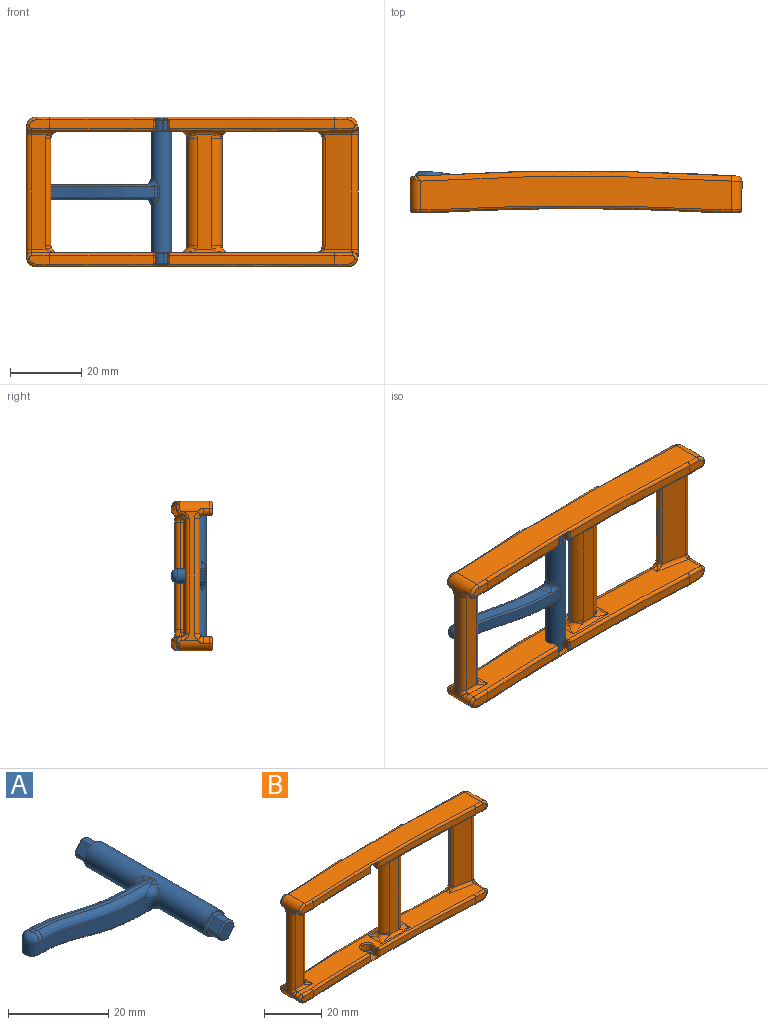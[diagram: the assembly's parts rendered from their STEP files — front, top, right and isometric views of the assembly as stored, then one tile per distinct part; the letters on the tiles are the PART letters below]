
ASSEMBLY  parts=2 mates=1
PART A: 70 faces, bbox 55.5x40.7x10.1 mm
  f0: cylinder r=2.9mm len=33.8mm, axis (0,1,0), area 564.6mm2, adj f1,f2,f36,f37,f38,f39,f40,f41
  f1: plane 5.8x5.8mm, normal (0,-1,0), area 5.9mm2, adj f0,f54,f56,f57,f59,f60,f61
  f2: plane 5.8x5.8mm, normal (0,1,0), area 5.9mm2, adj f0,f62,f63,f64,f65
  f3: plane 3.75x3.75mm, normal (0,1,0), area 9.4mm2, adj f66,f67,f68,f69
  f4: cylinder r=2.27mm len=2.76mm, axis (0,1,0), area 11mm2, adj f5,f7,f64,f67
  f5: plane 2.65x2.13mm, normal (-0.77,0,0.64), area 7.4mm2, adj f4,f6,f62,f69
  f6: cylinder r=2.27mm len=2.76mm, axis (0,1,0), area 11mm2, adj f5,f7,f63,f68
  f7: plane 2.65x2.13mm, normal (0.77,0,-0.64), area 7.4mm2, adj f4,f6,f65,f66
  f8: plane 2.65x2.02mm, normal (0.77,0,-0.64), area 7mm2, adj f9,f53,f58,f61
  f9: cylinder r=2.27mm len=2.76mm, axis (0,1,0), area 11mm2, adj f8,f10,f50,f59
  f10: plane 2.65x2.02mm, normal (-0.77,0,0.64), area 7mm2, adj f9,f48,f51,f56
  f11: cylinder r=2.27mm len=2.65mm, axis (0,1,0), area 10.2mm2, adj f51,f52,f57,f58
  f12: plane 3.75x3.75mm, normal (0,-1,0), area 9.4mm2, adj f48,f50,f52,f53
  f13: plane 3x1.02mm, normal (0,0,-1), area 3mm2, adj f18,f22,f28,f39
  f14: plane 1.02x0.8mm, normal (0,0,1), area 0.8mm2, adj f15,f29,f35,f44
  f15: extruded ~31.5x4.1mm, area 25.5mm2, adj f14,f16,f30,f34
  f16: plane 1.4x0.8mm, normal (0,0,1), area 1.1mm2, adj f15,f31,f32,f33
  f17: plane 3x2.5mm, normal (0,0,-1), area 6.5mm2, adj f18,f24,f25,f26
  f18: extruded ~31.5x4.8mm, area 96mm2, adj f13,f17,f23,f27
  f19: plane 30.17x7.59mm, normal (0,-1,0), area 93.1mm2, adj f21,f23,f24,f30,f31,f38
  f20: plane 30.17x7.58mm, normal (0,1,0), area 93.1mm2, adj f21,f26,f27,f33,f34,f45
  f21: cylinder r=2mm len=4mm, axis (0,0,-1), area 17.6mm2, adj f19,f20,f25,f32
  f22: cylinder r=0.5mm len=1.02mm, axis (-1,0,0), area 0.1mm2, adj f13,f23,f37
  f23: bspline ~49.02x5.3mm, area 24.5mm2, adj f18,f19,f22,f24,f36
  f24: cylinder r=0.5mm len=1mm, axis (-1,0,0), area 0.8mm2, adj f17,f19,f23,f25
  f25: torus R=1.5mm, axis (0,0,1), area 4.5mm2, adj f17,f21,f24,f26
  f26: cylinder r=0.5mm len=1mm, axis (1,0,0), area 0.8mm2, adj f17,f20,f25,f27
  f27: bspline ~43.19x5.3mm, area 24.5mm2, adj f18,f20,f26,f28,f43
  f28: cylinder r=0.5mm len=1.02mm, axis (1,0,0), area 0.1mm2, adj f13,f27,f41
  f29: cylinder r=1.6mm len=1.02mm, axis (1,0,0), area 0.3mm2, adj f14,f30,f42
  f30: bspline ~42.04x5.7mm, area 77.6mm2, adj f15,f19,f29,f31,f40
  f31: cylinder r=1.6mm len=1.6mm, axis (1,0,0), area 2.5mm2, adj f16,f19,f30,f32
  f32: torus R=0.4mm, axis (0,0,1), area 11.2mm2, adj f16,f21,f31,f33
  f33: cylinder r=1.6mm len=1.6mm, axis (-1,0,0), area 2.5mm2, adj f16,f20,f32,f34
  f34: bspline ~42.11x5.7mm, area 77.6mm2, adj f15,f20,f33,f35,f47
  f35: cylinder r=1.6mm len=1.02mm, axis (-1,0,0), area 0.3mm2, adj f14,f34,f46
  f36: bspline ~3.58x2.3mm, area 4.3mm2, adj f0,f23,f37,f38
  f37: bspline ~1.72x1.59mm, area 0.9mm2, adj f0,f22,f36,f39
  f38: torus R=4.9mm, axis (0,-1,0), area 8.4mm2, adj f0,f19,f36,f40
  f39: cylinder r=2mm len=3mm, axis (0,1,0), area 1.2mm2, adj f0,f13,f37,f41
  f40: bspline ~3.88x3.08mm, area 6.5mm2, adj f0,f30,f38,f42
  f41: bspline ~1.72x1.59mm, area 0.9mm2, adj f0,f28,f39,f43
  f42: bspline ~2.46x2.24mm, area 1mm2, adj f0,f29,f40,f44
  f43: bspline ~3.58x2.3mm, area 4.3mm2, adj f0,f27,f41,f45
  f44: cylinder r=2mm len=0.8mm, axis (0,1,0), area 0.3mm2, adj f0,f14,f42,f46
  f45: torus R=4.9mm, axis (0,-1,0), area 8.4mm2, adj f0,f20,f43,f47
  f46: bspline ~1.9x1.63mm, area 1mm2, adj f0,f35,f44,f47
  f47: bspline ~3.88x3.08mm, area 6.5mm2, adj f0,f34,f45,f46
  f48: cylinder r=0.4mm len=2.28mm, axis (0.64,0,0.77), area 1.6mm2, adj f10,f12,f49,f50
  f49: sphere r=0.4mm, area 0.1mm2, adj f48,f51,f52
  f50: torus R=1.88mm, axis (0,-1,0), area 2.4mm2, adj f9,f12,f48,f53
  f51: cylinder r=0.4mm len=2.65mm, axis (0,1,0), area 0.8mm2, adj f10,f11,f49,f54
  f52: torus R=1.88mm, axis (0,-1,0), area 2.3mm2, adj f11,f12,f49,f55
  f53: cylinder r=0.4mm len=2.28mm, axis (-0.64,0,-0.77), area 1.6mm2, adj f8,f12,f50,f55
  f54: torus R=0.8mm, axis (0,-1,0), area 0.2mm2, adj f1,f51,f56,f57
  f55: sphere r=0.4mm, area 0.1mm2, adj f52,f53,f58
  f56: cylinder r=0.4mm len=2.38mm, axis (0.64,0,0.77), area 1.7mm2, adj f1,f10,f54,f59
  f57: torus R=2.67mm, axis (0,-1,0), area 2.6mm2, adj f1,f11,f54,f60
  f58: cylinder r=0.4mm len=2.65mm, axis (0,1,0), area 0.8mm2, adj f8,f11,f55,f60
  f59: torus R=2.67mm, axis (0,-1,0), area 2.9mm2, adj f1,f9,f56,f61
  f60: torus R=0.8mm, axis (0,-1,0), area 0.2mm2, adj f1,f57,f58,f61
  f61: cylinder r=0.4mm len=2.38mm, axis (-0.64,0,-0.77), area 1.7mm2, adj f1,f8,f59,f60
  f62: cylinder r=0.4mm len=2.59mm, axis (-0.64,0,-0.77), area 1.8mm2, adj f2,f5,f63,f64
  f63: torus R=2.67mm, axis (0,-1,0), area 2.9mm2, adj f2,f6,f62,f65
  f64: torus R=2.67mm, axis (0,-1,0), area 2.9mm2, adj f2,f4,f62,f65
  f65: cylinder r=0.4mm len=2.59mm, axis (0.64,0,0.77), area 1.8mm2, adj f2,f7,f63,f64
  f66: cylinder r=0.4mm len=2.39mm, axis (0.64,0,0.77), area 1.7mm2, adj f3,f7,f67,f68
  f67: torus R=1.88mm, axis (0,-1,0), area 2.4mm2, adj f3,f4,f66,f69
  f68: torus R=1.88mm, axis (0,-1,0), area 2.4mm2, adj f3,f6,f66,f69
  f69: cylinder r=0.4mm len=2.39mm, axis (-0.64,0,-0.77), area 1.7mm2, adj f3,f5,f67,f68
PART B: 187 faces, bbox 94.1x13x42.5 mm
  f0: cylinder r=721.5mm len=29.22mm, axis (0,0,-1), area 70.1mm2, adj f27,f65,f67,f178,f185
  f1: plane 2.6x1.64mm, normal (1,-0.07,0), area 4.2mm2, adj f21,f62,f66,f67,f176
  f2: plane 2.6x1.59mm, normal (-1,-0.07,0), area 4.1mm2, adj f21,f57,f58,f61,f174
  f3: cylinder r=721.5mm len=46.31mm, axis (0,0,-1), area 111.1mm2, adj f29,f46,f49,f162,f172
  f4: plane 2.6x1.59mm, normal (-1,-0.07,0), area 4.1mm2, adj f20,f46,f47,f48,f161
  f5: plane 2.6x1.64mm, normal (1,-0.07,0), area 4.2mm2, adj f20,f53,f54,f56,f163
  f6: plane 16x5.17mm, normal (0,1,0), area 69.1mm2, adj f42,f44,f92,f123,f124,f131
  f7: plane 5.61x2.4mm, normal (0,-1,0), area 12.5mm2, adj f25,f167,f169,f171,f173
  f8: plane 30x1.5mm, normal (1,0,0), area 43.3mm2, adj f37,f39,f41,f74,f75,f120,f123,f146
  f9: cylinder r=721.5mm len=46.31mm, axis (0,0,-1), area 111.1mm2, adj f28,f58,f60,f175,f185
  f10: plane 36x4.5mm, normal (-1,0,0), area 56.9mm2, adj f76,f79,f130,f131,f132,f139,f140,f141
  f11: plane 87x9.31mm, normal (0,0,-1), area 712.6mm2, adj f76,f77,f83,f183,f185,f186
  f12: plane 36x1.78mm, normal (1,0,0), area 28.7mm2, adj f77,f78,f82,f151,f152,f153
  f13: plane 90.41x9.31mm, normal (0,0,-1), area 547.8mm2, adj f48,f51,f54,f68,f69,f72,f75,f89
  f14: plane 90.41x9.31mm, normal (0,0,1), area 547.8mm2, adj f61,f64,f66,f70,f71,f73,f74,f85
  f15: plane 87x9.31mm, normal (0,0,1), area 712.6mm2, adj f78,f79,f80,f170,f172,f173
  f16: plane 5.12x3.9mm, normal (0,0,-1), area 15.8mm2, adj f47,f50,f52,f53
  f17: plane 5.12x3.9mm, normal (0,0,1), area 15.8mm2, adj f57,f59,f62,f63
  f18: plane 30x0.18mm, normal (-1,0,0), area 5.3mm2, adj f69,f70,f87,f158
  f19: plane 32x7.57mm, normal (-0.2,-0.98,0), area 241.7mm2, adj f98,f99,f152,f157,f158,f159
  f20: cylinder r=2.35mm len=4.7mm, axis (0,0,1), area 28.1mm2, adj f4,f5,f50,f51
  f21: cylinder r=2.35mm len=4.7mm, axis (0,0,1), area 28.1mm2, adj f1,f2,f59,f64
  f22: plane 16x5.17mm, normal (0,1,0), area 69.1mm2, adj f44,f45,f93,f120,f121,f131
  f23: plane 32x4.2mm, normal (0,1,0), area 128.1mm2, adj f90,f91,f104,f106,f108,f113,f115,f117
  f24: plane 32x4.2mm, normal (0,-1,0), area 128.1mm2, adj f96,f97,f101,f103,f105,f112,f114,f116
  f25: cylinder r=721.5mm len=29.22mm, axis (0,0,-1), area 70.1mm2, adj f7,f55,f56,f165,f172
  f26: cylinder r=721.5mm len=90.59mm, axis (0,0,-1), area 443.7mm2, adj f80,f81,f82,f83,f84,f85,f86,f87
  f27: plane 5.61x2.4mm, normal (0,-1,0), area 12.5mm2, adj f0,f180,f182,f184,f186
  f28: plane 5.61x2.4mm, normal (0,-1,0), area 12.5mm2, adj f9,f177,f179,f181,f183
  f29: plane 5.61x2.4mm, normal (0,-1,0), area 12.5mm2, adj f3,f164,f166,f168,f170
  f30: plane 3.15x0.2mm, normal (0,0,1), area 0.6mm2, adj f31,f35,f40,f42
  f31: cylinder r=2.05mm len=4.1mm, axis (0,1,0), area 1.3mm2, adj f30,f32,f36,f44
  f32: plane 3.15x0.2mm, normal (0,0,-1), area 0.6mm2, adj f31,f38,f43,f45
  f33: plane 4.8x3.3mm, normal (0,1,0), area 14.7mm2, adj f35,f36,f38,f39
  f34: plane 32x4.15mm, normal (0,-1,0), area 128.1mm2, adj f94,f95,f140,f145,f146,f147
  f35: cylinder r=0.4mm len=3.15mm, axis (-1,0,0), area 2mm2, adj f30,f33,f36,f37
  f36: torus R=1.65mm, axis (0,1,0), area 3.8mm2, adj f31,f33,f35,f38
  f37: torus R=0.8mm, axis (1,0,0), area 0.5mm2, adj f8,f35,f39,f40,f123
  f38: cylinder r=0.4mm len=3.15mm, axis (1,0,0), area 2mm2, adj f32,f33,f36,f41
  f39: cylinder r=0.4mm len=3.3mm, axis (0,0,-1), area 2.1mm2, adj f8,f33,f37,f41
  f40: cylinder r=0.4mm len=0.32mm, axis (0,-1,0), area 0.1mm2, adj f30,f37,f42,f123
  f41: torus R=0.8mm, axis (1,0,0), area 0.5mm2, adj f8,f38,f39,f43,f120
  f42: cylinder r=0.4mm len=3.26mm, axis (1,0,0), area 1.9mm2, adj f6,f30,f40,f44,f123
  f43: cylinder r=0.4mm len=0.32mm, axis (0,1,0), area 0.1mm2, adj f32,f41,f45,f120
  f44: torus R=2.45mm, axis (0,1,0), area 4.3mm2, adj f6,f22,f31,f42,f45
  f45: cylinder r=0.4mm len=3.26mm, axis (-1,0,0), area 1.9mm2, adj f22,f32,f43,f44,f120
  f46: cylinder r=0.4mm len=2.2mm, axis (0,0,-1), area 1.3mm2, adj f3,f4,f49,f161
  f47: cylinder r=0.4mm len=1.8mm, axis (0.07,-1,0), area 1mm2, adj f4,f16,f49,f50
  f48: cylinder r=0.4mm len=1.22mm, axis (-0.07,1,0), area 0.7mm2, adj f4,f13,f51,f161
  f49: bspline ~0.98x0.94mm, area 0.4mm2, adj f3,f46,f47,f52,f172
  f50: torus R=1.95mm, axis (0,0,1), area 6.5mm2, adj f16,f20,f47,f53
  f51: torus R=2.75mm, axis (0,0,-1), area 7.1mm2, adj f13,f20,f48,f54
  f52: torus R=721.9mm, axis (0,0,1), area 1.1mm2, adj f16,f49,f55,f172
  f53: cylinder r=0.4mm len=1.85mm, axis (0.07,1,0), area 1.1mm2, adj f5,f16,f50,f55
  f54: cylinder r=0.4mm len=1.27mm, axis (-0.07,-1,0), area 0.7mm2, adj f5,f13,f51,f163
  f55: bspline ~0.98x0.94mm, area 0.4mm2, adj f25,f52,f53,f56,f172
  f56: cylinder r=0.4mm len=2.2mm, axis (0,0,-1), area 1.3mm2, adj f5,f25,f55,f163
  f57: cylinder r=0.4mm len=1.8mm, axis (-0.07,1,0), area 1mm2, adj f2,f17,f59,f60
  f58: cylinder r=0.4mm len=2.2mm, axis (0,0,-1), area 1.3mm2, adj f2,f9,f60,f174
  f59: torus R=1.95mm, axis (0,0,1), area 6.5mm2, adj f17,f21,f57,f62
  f60: bspline ~0.98x0.94mm, area 0.4mm2, adj f9,f57,f58,f63,f185
  f61: cylinder r=0.4mm len=1.22mm, axis (0.07,-1,0), area 0.7mm2, adj f2,f14,f64,f174
  f62: cylinder r=0.4mm len=1.85mm, axis (-0.07,-1,0), area 1.1mm2, adj f1,f17,f59,f65
  f63: torus R=721.9mm, axis (0,0,1), area 1.1mm2, adj f17,f60,f65,f185
  f64: torus R=2.75mm, axis (0,0,1), area 7.1mm2, adj f14,f21,f61,f66
  f65: bspline ~0.98x0.94mm, area 0.4mm2, adj f0,f62,f63,f67,f185
  f66: cylinder r=0.4mm len=1.27mm, axis (0.07,1,0), area 0.7mm2, adj f1,f14,f64,f176
  f67: cylinder r=0.4mm len=2.2mm, axis (0,0,-1), area 1.3mm2, adj f0,f1,f65,f176
  f68: cylinder r=2mm len=6.5mm, axis (0,-1,0), area 5.5mm2, adj f13,f118,f119
  f69: cylinder r=2mm len=2mm, axis (0,1,0), area 2mm2, adj f13,f18,f88,f159,f160
  f70: cylinder r=2mm len=2mm, axis (0,1,0), area 2mm2, adj f14,f18,f86,f156,f157
  f71: cylinder r=2mm len=6.5mm, axis (0,-1,0), area 5.5mm2, adj f14,f110,f111
  f72: cylinder r=2mm len=6.5mm, axis (0,1,0), area 5.5mm2, adj f13,f107,f109
  f73: cylinder r=2mm len=6.5mm, axis (0,1,0), area 5.5mm2, adj f14,f100,f102
  f74: cylinder r=2mm len=6mm, axis (0,-1,0), area 8.9mm2, adj f8,f14,f124,f125,f144,f145
  f75: cylinder r=2mm len=6mm, axis (0,-1,0), area 8.9mm2, adj f8,f13,f121,f122,f147,f148
  f76: cylinder r=3mm len=8.42mm, axis (0,1,0), area 36.3mm2, adj f10,f11,f126,f127,f128,f129,f137,f138
  f77: cylinder r=3mm len=7.99mm, axis (0,1,0), area 32mm2, adj f11,f12,f84,f149,f150,f181
  f78: cylinder r=3mm len=7.99mm, axis (0,1,0), area 32mm2, adj f12,f15,f81,f154,f155,f168
  f79: cylinder r=3mm len=8.42mm, axis (0,1,0), area 36.3mm2, adj f10,f15,f133,f134,f135,f136,f142,f143
  f80: torus R=720mm, axis (0,0,-1), area 206.9mm2, adj f15,f26,f81,f136
  f81: bspline ~3.67x3.67mm, area 8.8mm2, adj f26,f78,f80,f82
  f82: cylinder r=1.5mm len=36mm, axis (0,0,-1), area 81.4mm2, adj f12,f26,f81,f84
  f83: torus R=720mm, axis (0,0,1), area 206.9mm2, adj f11,f26,f84,f126
  f84: bspline ~3.67x3.67mm, area 8.8mm2, adj f26,f77,f82,f83
  f85: torus R=720mm, axis (0,0,1), area 188.7mm2, adj f14,f26,f86,f128
  f86: bspline ~4.28x3.71mm, area 9.6mm2, adj f26,f70,f85,f87
  f87: cylinder r=1.5mm len=30mm, axis (0,0,-1), area 73.1mm2, adj f18,f26,f86,f88
  f88: bspline ~4.29x4.28mm, area 9.6mm2, adj f26,f69,f87,f89
  f89: torus R=720mm, axis (0,0,-1), area 188.7mm2, adj f13,f26,f88,f134
  f90: cylinder r=1mm len=14mm, axis (-1,0,0), area 14.3mm2, adj f13,f23,f109,f119
  f91: cylinder r=1mm len=14mm, axis (-1,0,0), area 14.3mm2, adj f14,f23,f102,f111
  f92: cylinder r=1mm len=8mm, axis (1,0,0), area 10.3mm2, adj f6,f14,f125,f130
  f93: cylinder r=1mm len=8mm, axis (1,0,0), area 10.3mm2, adj f13,f22,f122,f132
  f94: cylinder r=1mm len=7.5mm, axis (1,0,0), area 9.1mm2, adj f14,f34,f138,f139,f144
  f95: cylinder r=1mm len=7.5mm, axis (1,0,0), area 9.1mm2, adj f13,f34,f141,f142,f148
  f96: cylinder r=1mm len=14mm, axis (1,0,0), area 14.3mm2, adj f13,f24,f107,f118
  f97: cylinder r=1mm len=14mm, axis (1,0,0), area 14.3mm2, adj f14,f24,f100,f110
  f98: cylinder r=1mm len=10.61mm, axis (-0.98,0.2,0), area 14.4mm2, adj f13,f19,f153,f154,f160
  f99: cylinder r=1mm len=10.61mm, axis (0.98,-0.2,0), area 14.4mm2, adj f14,f19,f150,f151,f156
  f100: bspline ~5x4mm, area 7.6mm2, adj f73,f97,f101,f102
  f101: torus R=5mm, axis (0,-1,0), area 2.6mm2, adj f24,f100,f103,f104
  f102: bspline ~5x4mm, area 7.6mm2, adj f73,f91,f100,f104
  f103: cylinder r=3mm len=30mm, axis (0,0,1), area 118.6mm2, adj f24,f101,f105,f106
  f104: torus R=5mm, axis (0,1,0), area 2.6mm2, adj f23,f101,f102,f106
  f105: torus R=5mm, axis (0,-1,0), area 2.6mm2, adj f24,f103,f107,f108
  f106: cylinder r=3mm len=30mm, axis (0,0,1), area 118.6mm2, adj f23,f103,f104,f108
  f107: bspline ~5x4mm, area 7.6mm2, adj f72,f96,f105,f109
  f108: torus R=5mm, axis (0,1,0), area 2.6mm2, adj f23,f105,f106,f109
  f109: bspline ~5x4mm, area 7.6mm2, adj f72,f90,f107,f108
  f110: bspline ~5x4mm, area 7.6mm2, adj f71,f97,f111,f112
  f111: bspline ~5x4mm, area 7.6mm2, adj f71,f91,f110,f113
  f112: torus R=5mm, axis (0,-1,0), area 2.6mm2, adj f24,f110,f113,f114
  f113: torus R=5mm, axis (0,1,0), area 2.6mm2, adj f23,f111,f112,f115
  f114: cylinder r=3mm len=30mm, axis (0,0,-1), area 118.6mm2, adj f24,f112,f115,f116
  f115: cylinder r=3mm len=30mm, axis (0,0,-1), area 118.6mm2, adj f23,f113,f114,f117
  f116: torus R=5mm, axis (0,-1,0), area 2.6mm2, adj f24,f114,f117,f118
  f117: torus R=5mm, axis (0,1,0), area 2.6mm2, adj f23,f115,f116,f119
  f118: bspline ~5x4mm, area 7.6mm2, adj f68,f96,f116,f119
  f119: bspline ~5x4mm, area 7.6mm2, adj f68,f90,f117,f118
  f120: cylinder r=1mm len=12.94mm, axis (0,0,-1), area 20.1mm2, adj f8,f22,f41,f43,f45,f121
  f121: torus R=3mm, axis (0,1,0), area 1.3mm2, adj f22,f75,f120,f122
  f122: bspline ~2.94x2mm, area 1.5mm2, adj f75,f93,f121
  f123: cylinder r=1mm len=12.94mm, axis (0,0,-1), area 20.1mm2, adj f6,f8,f37,f40,f42,f124
  f124: torus R=3mm, axis (0,1,0), area 1.3mm2, adj f6,f74,f123,f125
  f125: bspline ~2.94x2mm, area 1.5mm2, adj f74,f92,f124
  f126: bspline ~2.32x1.85mm, area 1.3mm2, adj f76,f83,f127
  f127: bspline ~2.58x1.99mm, area 2.4mm2, adj f26,f76,f126,f128
  f128: bspline ~2.1x1.84mm, area 3mm2, adj f76,f85,f127,f129
  f129: cylinder r=1mm len=1mm, axis (0,-1,0), area 0.1mm2, adj f14,f76,f128,f130
  f130: torus R=2mm, axis (1,0,0), area 3.4mm2, adj f10,f92,f129,f131
  f131: cylinder r=1mm len=32mm, axis (0,0,1), area 50.3mm2, adj f6,f10,f22,f130,f132
  f132: torus R=2mm, axis (1,0,0), area 3.4mm2, adj f10,f93,f131,f133
  f133: cylinder r=1mm len=1mm, axis (0,1,0), area 0.1mm2, adj f13,f79,f132,f134
  f134: bspline ~1.84x1.84mm, area 3mm2, adj f79,f89,f133,f135
  f135: bspline ~2.58x1.99mm, area 2.4mm2, adj f26,f79,f134,f136
  f136: bspline ~2.32x1.85mm, area 1.3mm2, adj f79,f80,f135
  f137: cylinder r=1.5mm len=2mm, axis (0,1,0), area 5.2mm2, adj f14,f76,f138,f182
  f138: bspline ~2.25x2.12mm, area 2.9mm2, adj f76,f94,f137,f139
  f139: torus R=2.5mm, axis (1,0,0), area 3.4mm2, adj f10,f94,f138,f140
  f140: cylinder r=1.5mm len=32mm, axis (0,0,1), area 75.4mm2, adj f10,f34,f139,f141
  f141: torus R=2.5mm, axis (1,0,0), area 3.4mm2, adj f10,f95,f140,f142
  f142: bspline ~2.43x2.31mm, area 2.9mm2, adj f79,f95,f141,f143
  f143: cylinder r=1.5mm len=2mm, axis (0,1,0), area 5.2mm2, adj f13,f79,f142,f169
  f144: bspline ~3.46x2.5mm, area 2.3mm2, adj f74,f94,f145
  f145: torus R=3.5mm, axis (0,-1,0), area 1.7mm2, adj f34,f74,f144,f146
  f146: cylinder r=1.5mm len=30mm, axis (0,0,-1), area 70.7mm2, adj f8,f34,f145,f147
  f147: torus R=3.5mm, axis (0,-1,0), area 1.7mm2, adj f34,f75,f146,f148
  f148: bspline ~3.46x2.5mm, area 2.3mm2, adj f75,f95,f147
  f149: cylinder r=1.5mm len=4.61mm, axis (0,1,0), area 13.2mm2, adj f14,f77,f150,f179
  f150: bspline ~2.66x2.4mm, area 3mm2, adj f77,f99,f149,f151
  f151: bspline ~2.65x2.12mm, area 3.6mm2, adj f12,f99,f150,f152
  f152: cylinder r=1.5mm len=32mm, axis (0,0,1), area 84.9mm2, adj f12,f19,f151,f153
  f153: bspline ~2x1.9mm, area 3.6mm2, adj f12,f98,f152,f154
  f154: bspline ~2.66x2.4mm, area 3mm2, adj f78,f98,f153,f155
  f155: cylinder r=1.5mm len=4.61mm, axis (0,1,0), area 13.2mm2, adj f13,f78,f154,f166
  f156: bspline ~2.75x1.6mm, area 1.3mm2, adj f70,f99,f157
  f157: bspline ~1.02x1mm, area 1.1mm2, adj f19,f70,f156,f158
  f158: cylinder r=1mm len=30mm, axis (0,0,1), area 41.2mm2, adj f18,f19,f157,f159
  f159: bspline ~1.02x1mm, area 1.1mm2, adj f19,f69,f158,f160
  f160: bspline ~2.75x1.6mm, area 1.3mm2, adj f69,f98,f159
  f161: bspline ~0.94x0.92mm, area 0.6mm2, adj f4,f46,f48,f162
  f162: torus R=722.3mm, axis (0,0,-1), area 58.2mm2, adj f3,f13,f161,f164
  f163: bspline ~0.94x0.91mm, area 0.6mm2, adj f5,f54,f56,f165
  f164: cylinder r=0.8mm len=4.91mm, axis (-1,0,0), area 6.2mm2, adj f13,f29,f162,f166
  f165: torus R=722.3mm, axis (0,0,-1), area 36.7mm2, adj f13,f25,f163,f167
  f166: torus R=0.7mm, axis (0,1,0), area 2.9mm2, adj f29,f155,f164,f168
  f167: cylinder r=0.8mm len=4.91mm, axis (1,0,0), area 6.2mm2, adj f7,f13,f165,f169
  f168: torus R=2.2mm, axis (0,1,0), area 4.2mm2, adj f29,f78,f166,f170
  f169: torus R=0.7mm, axis (0,1,0), area 2.9mm2, adj f7,f143,f167,f171
  f170: cylinder r=0.8mm len=3.49mm, axis (1,0,0), area 4.4mm2, adj f15,f29,f168,f172
  f171: torus R=2.2mm, axis (0,1,0), area 4.2mm2, adj f7,f79,f169,f173
  f172: torus R=722.3mm, axis (0,0,-1), area 99.2mm2, adj f3,f15,f25,f49,f52,f55,f170,f173
  f173: cylinder r=0.8mm len=3.49mm, axis (1,0,0), area 4.4mm2, adj f7,f15,f171,f172
  f174: bspline ~0.94x0.91mm, area 0.6mm2, adj f2,f58,f61,f175
  f175: torus R=722.3mm, axis (0,0,1), area 58.2mm2, adj f9,f14,f174,f177
  f176: bspline ~0.94x0.91mm, area 0.6mm2, adj f1,f66,f67,f178
  f177: cylinder r=0.8mm len=4.91mm, axis (1,0,0), area 6.2mm2, adj f14,f28,f175,f179
  f178: torus R=722.3mm, axis (0,0,1), area 36.7mm2, adj f0,f14,f176,f180
  f179: torus R=0.7mm, axis (0,1,0), area 2.9mm2, adj f28,f149,f177,f181
  f180: cylinder r=0.8mm len=4.91mm, axis (1,0,0), area 6.2mm2, adj f14,f27,f178,f182
  f181: torus R=2.2mm, axis (0,1,0), area 4.2mm2, adj f28,f77,f179,f183
  f182: torus R=0.7mm, axis (0,1,0), area 2.9mm2, adj f27,f137,f180,f184
  f183: cylinder r=0.8mm len=3.49mm, axis (1,0,0), area 4.4mm2, adj f11,f28,f181,f185
  f184: torus R=2.2mm, axis (0,1,0), area 4.2mm2, adj f27,f76,f182,f186
  f185: torus R=722.3mm, axis (0,0,1), area 99.2mm2, adj f0,f9,f11,f60,f63,f65,f183,f186
  f186: cylinder r=0.8mm len=3.49mm, axis (1,0,0), area 4.4mm2, adj f11,f27,f184,f185
PLACE A rot(axis=(-1,0,0),90deg) t=(-8.55,-7,0)mm
PLACE B at identity fixed
MATE revolute A.f0 <-> B.f51  axis (0,0,-1) through (-8.55,-7,0)mm
